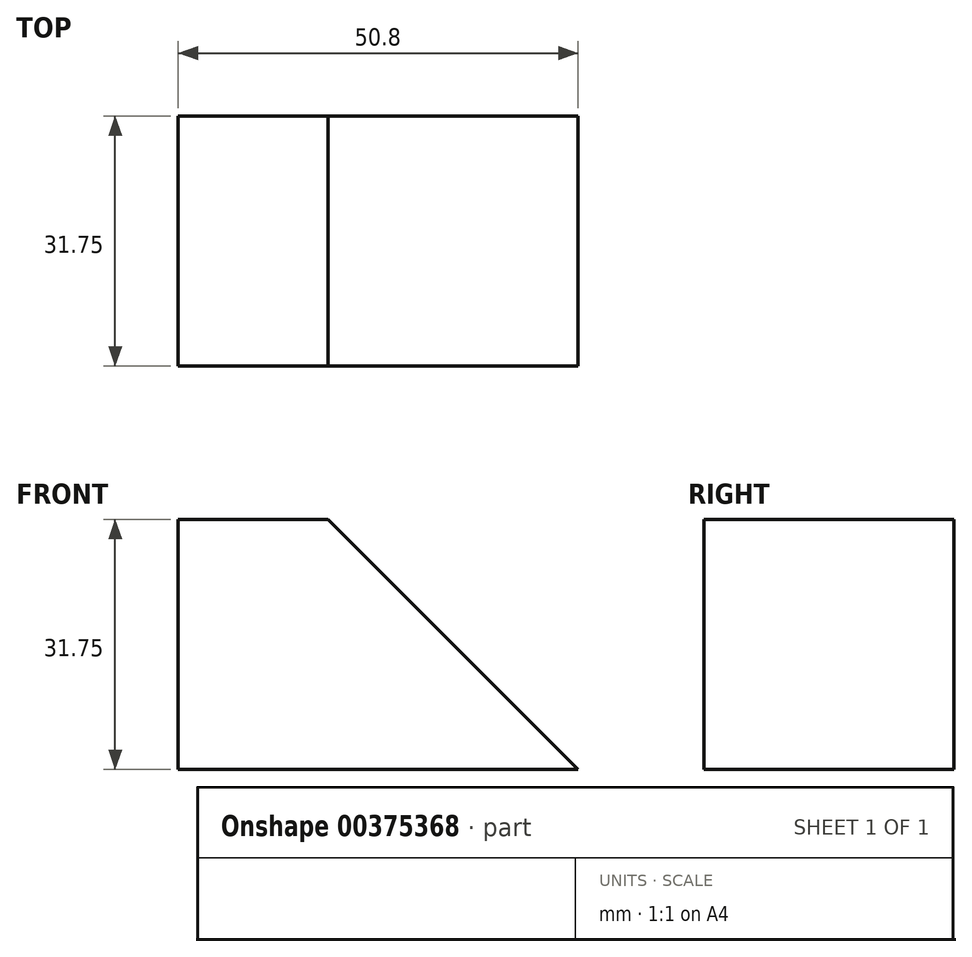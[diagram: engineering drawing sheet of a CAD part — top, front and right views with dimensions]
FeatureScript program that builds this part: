
annotation { "Feature Type Name" : "Feature", "Feature Type Description" : "" }
export const myFeature = defineFeature(function(context is Context, id is Id, definition is map)
    precondition{}
    {
        {
            var Q0;
            Q0=qCreatedBy(makeId("Front.planeOp"),FACE);
            var sketch = newSketch(context, id + "F0", { "sketchPlane" : qUnion([Q0])});
            skLineSegment(sketch, "E0", {"start": v(0, 0) * mm, "end": v(0, 31.75) * mm});
            skLineSegment(sketch, "E1", {"start": v(0, 31.75) * mm, "end": v(19.05, 31.75) * mm});
            skLineSegment(sketch, "E2", {"start": v(19.05, 31.75) * mm, "end": v(50.8, 0) * mm});
            skLineSegment(sketch, "E3", {"start": v(50.8, 0) * mm, "end": v(0, 0) * mm});
            skSolve(sketch);
        }
        {
            var Q0;
            Q0 = qSketchRegion(id + "F0", true);
            extrude(context, id + "F1", {"entities" : qUnion([Q0]), "depth" : 31.75 * mm});
        }
    });
